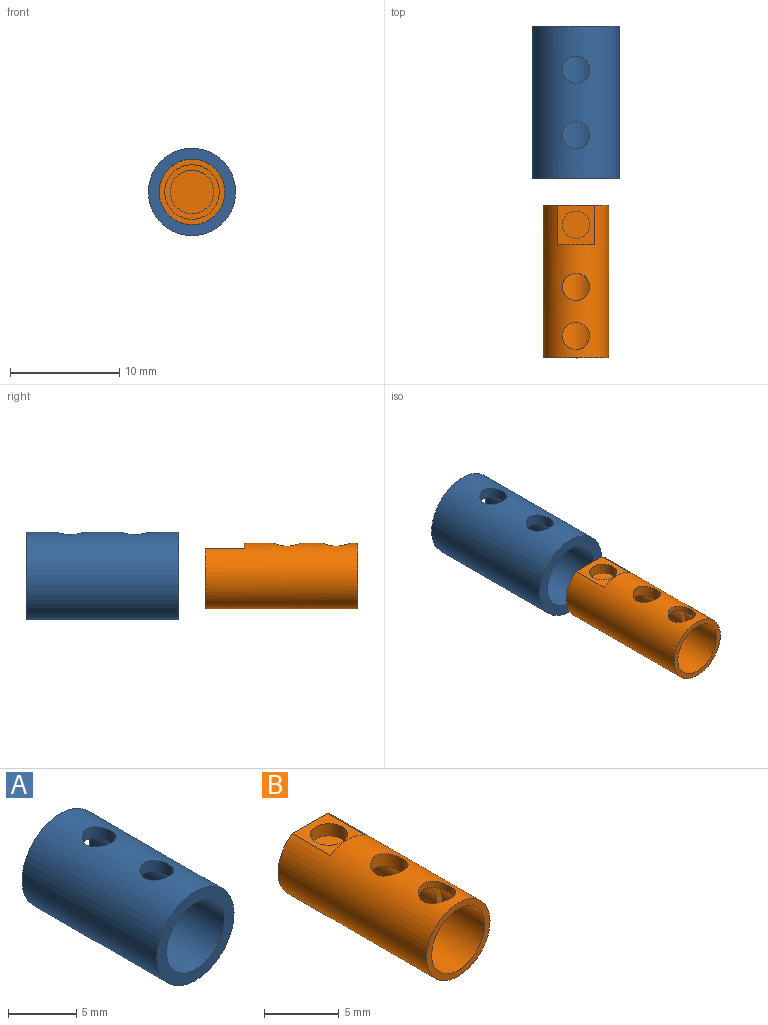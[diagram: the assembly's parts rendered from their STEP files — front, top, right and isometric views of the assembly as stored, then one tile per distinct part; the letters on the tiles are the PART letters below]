
ASSEMBLY  parts=2 mates=1
PART A: 6 faces, bbox 8x14x8 mm
  f0: cylinder r=4mm len=14mm, axis (0,-1,0), area 341.9mm2, adj f2,f3,f4,f5
  f1: cylinder r=3mm len=14mm, axis (0,-1,0), area 253.9mm2, adj f2,f3,f4,f5
  f2: plane 8x8mm, normal (0,1,0), area 22mm2, adj f0,f1
  f3: plane 8x8mm, normal (0,-1,0), area 22mm2, adj f0,f1
  f4: cylinder r=1.25mm len=2.5mm, axis (0,0,1), area 8.1mm2, adj f0,f1
  f5: cylinder r=1.25mm len=2.5mm, axis (0,0,1), area 8.1mm2, adj f0,f1
PART B: 13 faces, bbox 6x14x6 mm
  f0: cylinder r=3mm len=14mm, axis (0,1,0), area 241.2mm2, adj f2,f3,f5,f6,f9,f10
  f1: cylinder r=2mm len=6mm, axis (0,-1,0), area 70.2mm2, adj f4,f6,f7
  f2: plane 6x6mm, normal (0,-1,0), area 8.6mm2, adj f0,f8
  f3: plane 6x5.5mm, normal (0,1,0), area 27.1mm2, adj f0,f10
  f4: plane 4x4mm, normal (0,-1,0), area 12.6mm2, adj f1
  f5: cylinder r=1.25mm len=2.5mm, axis (0,0,1), area 4.2mm2, adj f0,f8
  f6: cylinder r=1.25mm len=2.5mm, axis (0,0,1), area 8.5mm2, adj f0,f1
  f7: plane 5x5mm, normal (0,-1,0), area 7.1mm2, adj f1,f8
  f8: cylinder r=2.5mm len=5mm, axis (0,-1,0), area 57.8mm2, adj f2,f5,f7
  f9: plane 3.32x0.5mm, normal (0,1,0), area 1.1mm2, adj f0,f10
  f10: plane 3.6x3.32mm, normal (0,0,1), area 7mm2, adj f0,f3,f9,f11
  f11: cylinder r=1.25mm len=2.5mm, axis (0,0,1), area 7.9mm2, adj f10,f12
  f12: plane 2.5x2.5mm, normal (0,0,1), area 4.9mm2, adj f11
PLACE A at identity fixed
PLACE B t=(0,1.09,0)mm
MATE slider B.f0 <-> A.f0  axis (0,1,0) through (0,-2.41,0)mm
